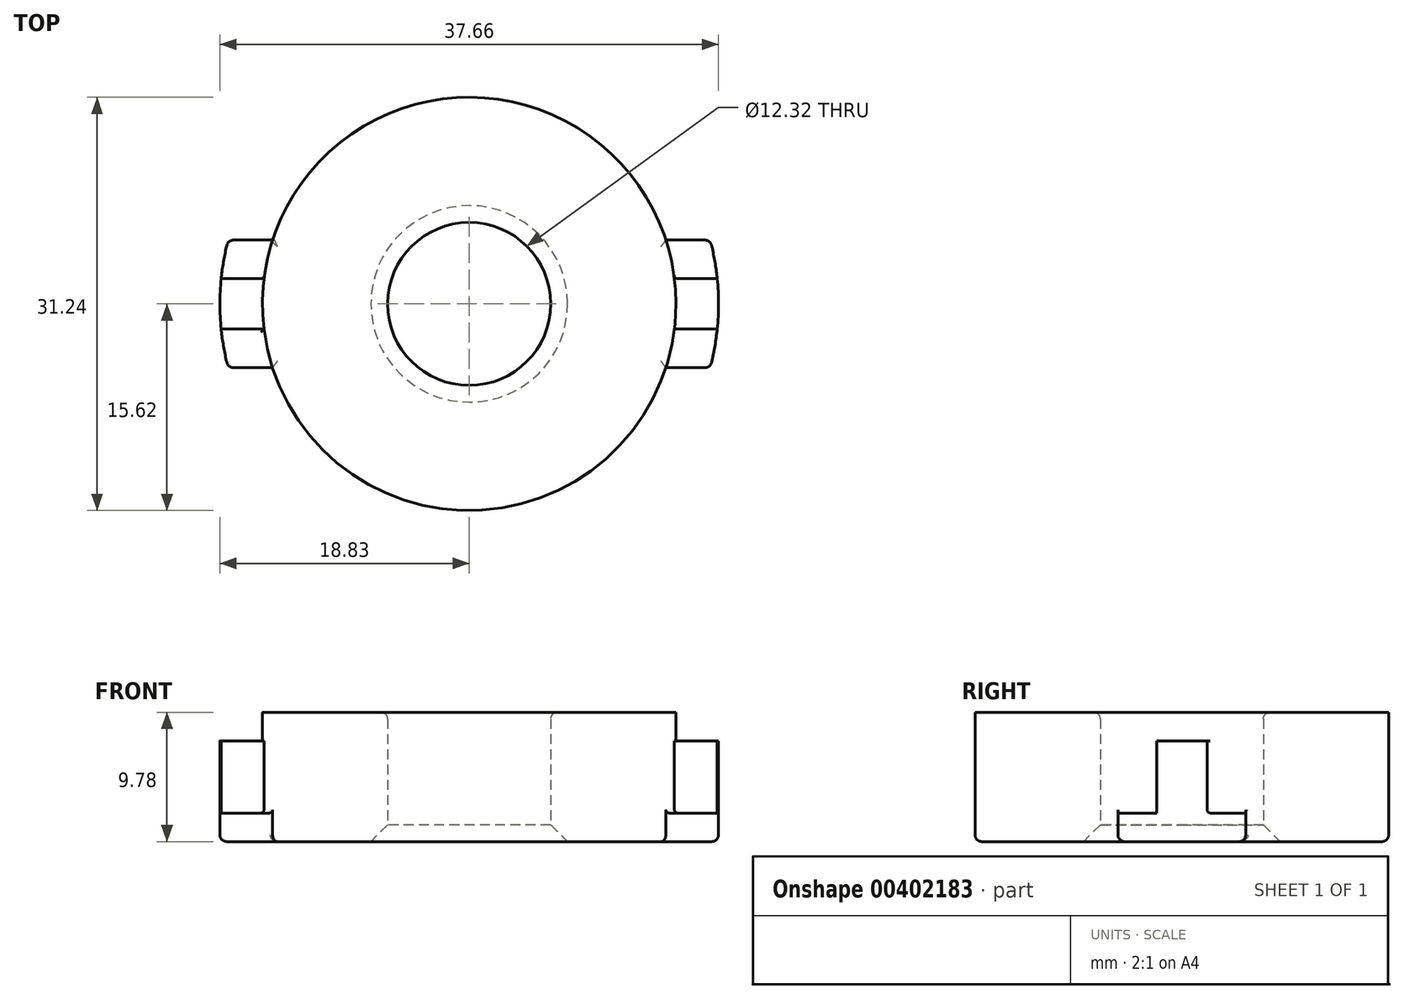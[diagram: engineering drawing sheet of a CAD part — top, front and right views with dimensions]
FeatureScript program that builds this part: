
annotation { "Feature Type Name" : "Feature", "Feature Type Description" : "" }
export const myFeature = defineFeature(function(context is Context, id is Id, definition is map)
    precondition{}
    {
        {
            var Q0;
            Q0=qCreatedBy(makeId("Top.planeOp"),FACE);
            var sketch = newSketch(context, id + "F0", { "sketchPlane" : qUnion([Q0])});
            skArc(sketch, "E0", {"start": v(-14.86, -4.83) * mm, "mid": v(0, -15.62) * mm, "end": v(14.86, -4.83) * mm});
            skCircle(sketch, "E1", {"center": v(0, 0) * mm, "radius": 6.16 * mm});
            skCircle(sketch, "E2", {"center": v(0, 0) * mm, "radius": 18.83 * mm, "construction": true});
            skLineSegment(sketch, "E3", {"start": v(-18.2, 4.83) * mm, "end": v(-14.86, 4.83) * mm});
            skLineSegment(sketch, "E4", {"start": v(-18.2, -4.83) * mm, "end": v(-14.86, -4.83) * mm});
            skArc(sketch, "E5", {"start": v(-18.2, 4.83) * mm, "mid": v(-18.83, 0) * mm, "end": v(-18.2, -4.83) * mm});
            skLineSegment(sketch, "E6.MirrorCS", {"start": v(18.2, 4.83) * mm, "end": v(14.86, 4.83) * mm});
            skLineSegment(sketch, "E7.MirrorCS", {"start": v(18.2, -4.83) * mm, "end": v(14.86, -4.83) * mm});
            skArc(sketch, "E8.MirrorCS", {"start": v(18.2, 4.83) * mm, "mid": v(18.83, 0) * mm, "end": v(18.2, -4.83) * mm});
            skArc(sketch, "E9.trimOffspring", {"start": v(14.86, 4.83) * mm, "mid": v(0, 15.62) * mm, "end": v(-14.86, 4.83) * mm});
            skSolve(sketch);
        }
        {
            var Q0;
            Q0=makeQuery(id+"F0.imprint","IMPRINT",FACE,{"disambiguationData":[TD([[makeQuery(id+"F0.imprint","IMPRINT",EDGE,{"derivedFrom":sQuery(id+"F0.wireOp",EDGE,"E0")}),1.0]])]});
            extrude(context, id + "F1", {"entities" : qUnion([Q0]), "depth" : 9.78 * mm});
        }
        {
            var Q0;
            Q0=makeQuery(id+"F1.opExtrude","CAP_FACE",FACE,{"disambiguationData":[OSD([sQuery(id+"F0.wireOp",EDGE,"E0"),sQuery(id+"F0.wireOp",EDGE,"E1"),sQuery(id+"F0.wireOp",EDGE,"E3"),sQuery(id+"F0.wireOp",EDGE,"E4"),sQuery(id+"F0.wireOp",EDGE,"E5"),sQuery(id+"F0.wireOp",EDGE,"E6.MirrorCS"),sQuery(id+"F0.wireOp",EDGE,"E7.MirrorCS"),sQuery(id+"F0.wireOp",EDGE,"E8.MirrorCS"),sQuery(id+"F0.wireOp",EDGE,"E9.trimOffspring")])],"isStart":false});
            var sketch = newSketch(context, id + "F2", { "sketchPlane" : qUnion([Q0])});
            skCircle(sketch, "E10", {"center": v(0, 0) * mm, "radius": 15.62 * mm});
            skCircle(sketch, "E11", {"center": v(0, 0) * mm, "radius": 21.37 * mm});
            skSolve(sketch);
        }
        {
            var Q0;
            {var subQ2=makeQuery(id+"F1.opExtrude","CAP_EDGE",EDGE,{"disambiguationData":[OSD([sQuery(id+"F0.wireOp",EDGE,"E3")])],"isStart":false});Q0=makeQuery(id+"F2.imprint","IMPRINT",FACE,{"disambiguationData":[TD([[makeQuery(id+"F2.imprint","IMPRINT",EDGE,{"derivedFrom":subQ2}),-1.0]])]});}
            var Q1;
            {var subQ2=makeQuery(id+"F1.opExtrude","CAP_EDGE",EDGE,{"disambiguationData":[OSD([sQuery(id+"F0.wireOp",EDGE,"E6.MirrorCS")])],"isStart":false});Q1=makeQuery(id+"F2.imprint","IMPRINT",FACE,{"disambiguationData":[TD([[makeQuery(id+"F2.imprint","IMPRINT",EDGE,{"derivedFrom":subQ2}),1.0]])]});}
            extrude(context, id + "F3", {"entities" : qUnion([Q0, Q1]), "operationType" : NewBodyOperationType.REMOVE, "oppositeDirection" : true, "depth" : 2.16 * mm});
        }
        {
            var Q0;
            Q0=makeQuery(id+"F3.boolean.opBoolean","COPY",FACE,{"derivedFrom":makeQuery(id+"F3.opExtrude","CAP_FACE",FACE,{"disambiguationData":[OSD([sQuery(id+"F0.wireOp",EDGE,"E3"),sQuery(id+"F0.wireOp",EDGE,"E4"),sQuery(id+"F0.wireOp",EDGE,"E5"),sQuery(id+"F2.wireOp",EDGE,"E10")])],"isStart":false})});
            var sketch = newSketch(context, id + "F4", { "sketchPlane" : qUnion([Q0])});
            skLineSegment(sketch, "E12", {"start": v(-15.5, 1.9) * mm, "end": v(-18.74, 1.9) * mm});
            skLineSegment(sketch, "E13", {"start": v(-15.5, -1.9) * mm, "end": v(-18.74, -1.9) * mm});
            skLineSegment(sketch, "E14.MirrorCS", {"start": v(15.5, 1.9) * mm, "end": v(18.74, 1.9) * mm});
            skLineSegment(sketch, "E15.MirrorCS", {"start": v(15.5, -1.9) * mm, "end": v(18.74, -1.9) * mm});
            skArc(sketch, "E16.0", {"start": v(18.2, 4.83) * mm, "mid": v(18.83, 0) * mm, "end": v(18.2, -4.83) * mm});
            skArc(sketch, "E16.1", {"start": v(14.86, -4.83) * mm, "mid": v(15.62, 0) * mm, "end": v(14.86, 4.83) * mm});
            skLineSegment(sketch, "E17.2", {"start": v(18.2, -4.83) * mm, "end": v(14.86, -4.83) * mm});
            skLineSegment(sketch, "E18.0", {"start": v(18.2, 4.83) * mm, "end": v(14.86, 4.83) * mm});
            skSolve(sketch);
        }
        {
            var Q0;
            {var subQ0=sQuery(id+"F4.wireOp",EDGE,"E14.MirrorCS");Q0=makeQuery(id+"F4.imprint","IMPRINT",FACE,{"disambiguationData":[TD([[makeQuery(id+"F4.imprint","IMPRINT",EDGE,{"derivedFrom":subQ0}),1.0]])]});}
            var Q1;
            {var subQ0=sQuery(id+"F4.wireOp",EDGE,"E15.MirrorCS");Q1=makeQuery(id+"F4.imprint","IMPRINT",FACE,{"disambiguationData":[TD([[makeQuery(id+"F4.imprint","IMPRINT",EDGE,{"derivedFrom":subQ0}),-1.0]])]});}
            var Q2;
            {var subQ0=sQuery(id+"F4.wireOp",EDGE,"E13");Q2=makeQuery(id+"F4.imprint","IMPRINT",FACE,{"disambiguationData":[TD([[makeQuery(id+"F4.imprint","IMPRINT",EDGE,{"derivedFrom":subQ0}),1.0]])]});}
            var Q3;
            {var subQ0=sQuery(id+"F4.wireOp",EDGE,"E12");Q3=makeQuery(id+"F4.imprint","IMPRINT",FACE,{"disambiguationData":[TD([[makeQuery(id+"F4.imprint","IMPRINT",EDGE,{"derivedFrom":subQ0}),-1.0]])]});}
            extrude(context, id + "F5", {"entities" : qUnion([Q0, Q1, Q2, Q3]), "operationType" : NewBodyOperationType.REMOVE, "oppositeDirection" : true, "depth" : 5.46 * mm});
        }
        {
            var Q0;
            Q0=makeQuery(id+"F3.boolean.opBoolean","COPY",EDGE,{"derivedFrom":makeQuery(id+"F3.opExtrude","CAP_EDGE",EDGE,{"disambiguationData":[OSD([sQuery(id+"F0.wireOp",EDGE,"E5")])],"isStart":false})});
            var Q1;
            Q1=makeQuery(id+"F5.boolean.opBoolean","COPY",EDGE,{"derivedFrom":makeQuery(id+"F5.opExtrude","CAP_EDGE",EDGE,{"disambiguationData":[OSD([sQuery(id+"F4.wireOp",EDGE,"E13")])],"isStart":true})});
            var Q2;
            Q2=makeQuery(id+"F5.boolean.opBoolean","COPY",EDGE,{"derivedFrom":makeQuery(id+"F5.opExtrude","CAP_EDGE",EDGE,{"disambiguationData":[OSD([sQuery(id+"F4.wireOp",EDGE,"E12")])],"isStart":true})});
            var Q3;
            Q3=makeQuery(id+"F5.boolean.opBoolean","COPY",EDGE,{"derivedFrom":makeQuery(id+"F5.opExtrude","SWEPT_EDGE",EDGE,{"disambiguationData":[OSD([sQuery(id+"F0.wireOp",EDGE,"E5"),sQuery(id+"F4.wireOp",EDGE,"E13")])]})});
            var Q4;
            {var subQ0=sQuery(id+"F0.wireOp",EDGE,"E5");var subQ1=makeQuery(id+"F3.boolean.opBoolean","COPY",EDGE,{"derivedFrom":makeQuery(id+"F3.opExtrude","CAP_EDGE",EDGE,{"disambiguationData":[OSD([subQ0])],"isStart":false})});Q4=makeQuery(id+"F5.boolean.opBoolean","COPY",EDGE,{"derivedFrom":makeQuery(id+"F5.opExtrude","CAP_EDGE",EDGE,{"disambiguationData":[OSD([subQ0]),TDD([makeQuery(id+"F4.imprint","IMPRINT",EDGE,{"disambiguationData":[TD([[makeQuery(id+"F4.imprint","INTERSECT",VERTEX,{"derivedFrom":[makeQuery(id+"F3.boolean.opBoolean","COPY",EDGE,{"derivedFrom":makeQuery(id+"F3.opExtrude","CAP_EDGE",EDGE,{"disambiguationData":[OSD([sQuery(id+"F0.wireOp",EDGE,"E4")])],"isStart":false})}),subQ1]}),1.0]])],"derivedFrom":subQ1})])],"isStart":false})});}
            var Q5;
            Q5=makeQuery(id+"F1.opExtrude","SWEPT_EDGE",EDGE,{"disambiguationData":[OSD([sQuery(id+"F0.wireOp",EDGE,"E4"),sQuery(id+"F0.wireOp",EDGE,"E5")])]});
            var Q6;
            Q6=makeQuery(id+"F5.boolean.opBoolean","COPY",EDGE,{"derivedFrom":makeQuery(id+"F5.opExtrude","CAP_EDGE",EDGE,{"disambiguationData":[OSD([sQuery(id+"F0.wireOp",EDGE,"E4")])],"isStart":false})});
            var Q7;
            Q7=makeQuery(id+"F1.opExtrude","CAP_EDGE",EDGE,{"disambiguationData":[OSD([sQuery(id+"F0.wireOp",EDGE,"E4")])],"isStart":true});
            var Q8;
            Q8=makeQuery(id+"F1.opExtrude","CAP_EDGE",EDGE,{"disambiguationData":[OSD([sQuery(id+"F0.wireOp",EDGE,"E5")])],"isStart":true});
            var Q9;
            Q9=makeQuery(id+"F1.opExtrude","CAP_EDGE",EDGE,{"disambiguationData":[OSD([sQuery(id+"F0.wireOp",EDGE,"E3")])],"isStart":true});
            var Q10;
            Q10=makeQuery(id+"F1.opExtrude","CAP_EDGE",EDGE,{"disambiguationData":[OSD([sQuery(id+"F0.wireOp",EDGE,"E9.trimOffspring")])],"isStart":true});
            var Q11;
            Q11=makeQuery(id+"F1.opExtrude","SWEPT_EDGE",EDGE,{"disambiguationData":[OSD([sQuery(id+"F0.wireOp",EDGE,"E3"),sQuery(id+"F0.wireOp",EDGE,"E5")])]});
            var Q12;
            Q12=makeQuery(id+"F5.boolean.opBoolean","COPY",EDGE,{"derivedFrom":makeQuery(id+"F5.opExtrude","SWEPT_EDGE",EDGE,{"disambiguationData":[OSD([sQuery(id+"F0.wireOp",EDGE,"E5"),sQuery(id+"F4.wireOp",EDGE,"E12")])]})});
            var Q13;
            Q13=makeQuery(id+"F1.opExtrude","CAP_EDGE",EDGE,{"disambiguationData":[OSD([sQuery(id+"F0.wireOp",EDGE,"E0")])],"isStart":true});
            var Q14;
            {var subQ0=sQuery(id+"F2.wireOp",EDGE,"E10");Q14=makeQuery(id+"F3.boolean.opBoolean","MERGE",EDGE,{"derivedFrom":[makeQuery(id+"F1.opExtrude","CAP_EDGE",EDGE,{"disambiguationData":[OSD([sQuery(id+"F0.wireOp",EDGE,"E0")])],"isStart":false}),makeQuery(id+"F1.opExtrude","CAP_EDGE",EDGE,{"disambiguationData":[OSD([sQuery(id+"F0.wireOp",EDGE,"E9.trimOffspring")])],"isStart":false}),makeQuery(id+"F3.opExtrude","CAP_EDGE",EDGE,{"disambiguationData":[OSD([subQ0]),TDD([makeQuery(id+"F2.imprint","IMPRINT",EDGE,{"disambiguationData":[TD([[makeQuery(id+"F2.imprint","INTERSECT",VERTEX,{"derivedFrom":[makeQuery(id+"F1.opExtrude","CAP_EDGE",EDGE,{"disambiguationData":[OSD([sQuery(id+"F0.wireOp",EDGE,"E4")])],"isStart":false}),subQ0]}),1.0]])],"derivedFrom":subQ0})])],"isStart":true}),makeQuery(id+"F3.opExtrude","CAP_EDGE",EDGE,{"disambiguationData":[OSD([subQ0]),TDD([makeQuery(id+"F2.imprint","IMPRINT",EDGE,{"disambiguationData":[TD([[makeQuery(id+"F2.imprint","INTERSECT",VERTEX,{"derivedFrom":[makeQuery(id+"F1.opExtrude","CAP_EDGE",EDGE,{"disambiguationData":[OSD([sQuery(id+"F0.wireOp",EDGE,"E7.MirrorCS")])],"isStart":false}),subQ0]}),-1.0]])],"derivedFrom":subQ0})])],"isStart":true})]});}
            var Q15;
            Q15=makeQuery(id+"F1.opExtrude","CAP_EDGE",EDGE,{"disambiguationData":[OSD([sQuery(id+"F0.wireOp",EDGE,"E7.MirrorCS")])],"isStart":true});
            var Q16;
            Q16=makeQuery(id+"F1.opExtrude","SWEPT_EDGE",EDGE,{"disambiguationData":[OSD([sQuery(id+"F0.wireOp",EDGE,"E7.MirrorCS"),sQuery(id+"F0.wireOp",EDGE,"E8.MirrorCS")])]});
            var Q17;
            {var subQ0=sQuery(id+"F4.wireOp",EDGE,"E16.0");Q17=makeQuery(id+"F5.boolean.opBoolean","COPY",EDGE,{"derivedFrom":makeQuery(id+"F5.opExtrude","CAP_EDGE",EDGE,{"disambiguationData":[OSD([subQ0]),TDD([makeQuery(id+"F4.imprint","IMPRINT",EDGE,{"disambiguationData":[TD([[makeQuery(id+"F4.imprint","INTERSECT",VERTEX,{"derivedFrom":[sQuery(id+"F4.wireOp",EDGE,"E15.MirrorCS"),subQ0]}),-1.0]])],"derivedFrom":subQ0})])],"isStart":false})});}
            var Q18;
            Q18=makeQuery(id+"F5.boolean.opBoolean","COPY",EDGE,{"derivedFrom":makeQuery(id+"F5.opExtrude","SWEPT_EDGE",EDGE,{"disambiguationData":[OSD([sQuery(id+"F4.wireOp",EDGE,"E15.MirrorCS"),sQuery(id+"F4.wireOp",EDGE,"E16.0")])]})});
            var Q19;
            Q19=makeQuery(id+"F3.boolean.opBoolean","COPY",EDGE,{"derivedFrom":makeQuery(id+"F3.opExtrude","CAP_EDGE",EDGE,{"disambiguationData":[OSD([sQuery(id+"F0.wireOp",EDGE,"E8.MirrorCS")])],"isStart":false})});
            var Q20;
            Q20=makeQuery(id+"F5.boolean.opBoolean","COPY",EDGE,{"derivedFrom":makeQuery(id+"F5.opExtrude","SWEPT_EDGE",EDGE,{"disambiguationData":[OSD([sQuery(id+"F4.wireOp",EDGE,"E14.MirrorCS"),sQuery(id+"F4.wireOp",EDGE,"E16.0")])]})});
            var Q21;
            {var subQ0=sQuery(id+"F4.wireOp",EDGE,"E16.0");Q21=makeQuery(id+"F5.boolean.opBoolean","COPY",EDGE,{"derivedFrom":makeQuery(id+"F5.opExtrude","CAP_EDGE",EDGE,{"disambiguationData":[OSD([subQ0]),TDD([makeQuery(id+"F4.imprint","IMPRINT",EDGE,{"disambiguationData":[TD([[makeQuery(id+"F4.imprint","INTERSECT",VERTEX,{"derivedFrom":[sQuery(id+"F4.wireOp",EDGE,"E14.MirrorCS"),subQ0]}),1.0]])],"derivedFrom":subQ0})])],"isStart":false})});}
            var Q22;
            Q22=makeQuery(id+"F1.opExtrude","SWEPT_EDGE",EDGE,{"disambiguationData":[OSD([sQuery(id+"F0.wireOp",EDGE,"E6.MirrorCS"),sQuery(id+"F0.wireOp",EDGE,"E8.MirrorCS")])]});
            var Q23;
            Q23=makeQuery(id+"F1.opExtrude","CAP_EDGE",EDGE,{"disambiguationData":[OSD([sQuery(id+"F0.wireOp",EDGE,"E8.MirrorCS")])],"isStart":true});
            var Q24;
            Q24=makeQuery(id+"F5.boolean.opBoolean","COPY",EDGE,{"derivedFrom":makeQuery(id+"F5.opExtrude","CAP_EDGE",EDGE,{"disambiguationData":[OSD([sQuery(id+"F4.wireOp",EDGE,"E15.MirrorCS")])],"isStart":true})});
            var Q25;
            Q25=makeQuery(id+"F5.boolean.opBoolean","COPY",EDGE,{"derivedFrom":makeQuery(id+"F5.opExtrude","CAP_EDGE",EDGE,{"disambiguationData":[OSD([sQuery(id+"F4.wireOp",EDGE,"E14.MirrorCS")])],"isStart":true})});
            var Q26;
            Q26=makeQuery(id+"F5.boolean.opBoolean","COPY",EDGE,{"derivedFrom":makeQuery(id+"F5.opExtrude","CAP_EDGE",EDGE,{"disambiguationData":[OSD([sQuery(id+"F4.wireOp",EDGE,"E18.0")])],"isStart":false})});
            var Q27;
            Q27=makeQuery(id+"F1.opExtrude","CAP_EDGE",EDGE,{"disambiguationData":[OSD([sQuery(id+"F0.wireOp",EDGE,"E6.MirrorCS")])],"isStart":true});
            var Q28;
            Q28=makeQuery(id+"F5.boolean.opBoolean","COPY",EDGE,{"derivedFrom":makeQuery(id+"F5.opExtrude","CAP_EDGE",EDGE,{"disambiguationData":[OSD([sQuery(id+"F0.wireOp",EDGE,"E3")])],"isStart":false})});
            var Q29;
            {var subQ0=sQuery(id+"F0.wireOp",EDGE,"E5");var subQ1=makeQuery(id+"F3.boolean.opBoolean","COPY",EDGE,{"derivedFrom":makeQuery(id+"F3.opExtrude","CAP_EDGE",EDGE,{"disambiguationData":[OSD([subQ0])],"isStart":false})});Q29=makeQuery(id+"F5.boolean.opBoolean","COPY",EDGE,{"derivedFrom":makeQuery(id+"F5.opExtrude","CAP_EDGE",EDGE,{"disambiguationData":[OSD([subQ0]),TDD([makeQuery(id+"F4.imprint","IMPRINT",EDGE,{"disambiguationData":[TD([[makeQuery(id+"F4.imprint","INTERSECT",VERTEX,{"derivedFrom":[makeQuery(id+"F3.boolean.opBoolean","COPY",EDGE,{"derivedFrom":makeQuery(id+"F3.opExtrude","CAP_EDGE",EDGE,{"disambiguationData":[OSD([sQuery(id+"F0.wireOp",EDGE,"E3")])],"isStart":false})}),subQ1]}),-1.0]])],"derivedFrom":subQ1})])],"isStart":false})});}
            var Q30;
            Q30=makeQuery(id+"F1.opExtrude","CAP_EDGE",EDGE,{"disambiguationData":[OSD([sQuery(id+"F0.wireOp",EDGE,"E1")])],"isStart":false});
            var Q31;
            Q31=makeQuery(id+"F5.boolean.opBoolean","COPY",EDGE,{"derivedFrom":makeQuery(id+"F5.opExtrude","CAP_EDGE",EDGE,{"disambiguationData":[OSD([sQuery(id+"F4.wireOp",EDGE,"E17.2")])],"isStart":false})});
            fillet(context, id + "F6", {"entities" : qUnion([Q0, Q1, Q2, Q3, Q4, Q5, Q6, Q7, Q8, Q9, Q10, Q11, Q12, Q13, Q14, Q15, Q16, Q17, Q18, Q19, Q20, Q21, Q22, Q23, Q24, Q25, Q26, Q27, Q28, Q29, Q30, Q31]), "radius" : 0.5 * mm, "tangentPropagation" : true, "allowEdgeOverflow" : false});
        }
        {
            var Q0;
            {var subQ0=sQuery(id+"F4.wireOp",EDGE,"E16.1");Q0=makeQuery(id+"F5.boolean.opBoolean","COPY",EDGE,{"derivedFrom":makeQuery(id+"F5.opExtrude","CAP_EDGE",EDGE,{"disambiguationData":[OSD([subQ0]),TDD([makeQuery(id+"F4.imprint","IMPRINT",EDGE,{"disambiguationData":[TD([[makeQuery(id+"F4.imprint","INTERSECT",VERTEX,{"derivedFrom":[sQuery(id+"F4.wireOp",EDGE,"E14.MirrorCS"),subQ0]}),-1.0]])],"derivedFrom":subQ0})])],"isStart":false})});}
            var Q1;
            Q1=makeQuery(id+"F5.boolean.opBoolean","COPY",EDGE,{"derivedFrom":makeQuery(id+"F5.opExtrude","CAP_EDGE",EDGE,{"disambiguationData":[OSD([sQuery(id+"F4.wireOp",EDGE,"E14.MirrorCS")])],"isStart":false})});
            var Q2;
            Q2=makeQuery(id+"F5.boolean.opBoolean","COPY",EDGE,{"derivedFrom":makeQuery(id+"F5.opExtrude","SWEPT_EDGE",EDGE,{"disambiguationData":[OSD([sQuery(id+"F4.wireOp",EDGE,"E14.MirrorCS"),sQuery(id+"F4.wireOp",EDGE,"E16.1")])]})});
            var Q3;
            {var subQ0=sQuery(id+"F4.wireOp",EDGE,"E16.1");Q3=makeQuery(id+"F5.boolean.opBoolean","COPY",EDGE,{"derivedFrom":makeQuery(id+"F5.opExtrude","CAP_EDGE",EDGE,{"disambiguationData":[OSD([subQ0]),TDD([makeQuery(id+"F4.imprint","IMPRINT",EDGE,{"disambiguationData":[TD([[makeQuery(id+"F4.imprint","INTERSECT",VERTEX,{"derivedFrom":[sQuery(id+"F4.wireOp",EDGE,"E15.MirrorCS"),subQ0]}),1.0]])],"derivedFrom":subQ0})])],"isStart":false})});}
            var Q4;
            Q4=makeQuery(id+"F1.opExtrude","SWEPT_EDGE",EDGE,{"disambiguationData":[OSD([sQuery(id+"F0.wireOp",EDGE,"E3"),sQuery(id+"F0.wireOp",EDGE,"E9.trimOffspring")])]});
            var Q5;
            Q5=makeQuery(id+"F5.boolean.opBoolean","COPY",EDGE,{"derivedFrom":makeQuery(id+"F5.opExtrude","CAP_EDGE",EDGE,{"disambiguationData":[OSD([sQuery(id+"F4.wireOp",EDGE,"E12")])],"isStart":false})});
            var Q6;
            Q6=makeQuery(id+"F5.boolean.opBoolean","COPY",EDGE,{"derivedFrom":makeQuery(id+"F5.opExtrude","SWEPT_EDGE",EDGE,{"disambiguationData":[OSD([sQuery(id+"F2.wireOp",EDGE,"E10"),sQuery(id+"F4.wireOp",EDGE,"E12")])]})});
            var Q7;
            Q7=makeQuery(id+"F5.boolean.opBoolean","COPY",EDGE,{"derivedFrom":makeQuery(id+"F5.opExtrude","CAP_EDGE",EDGE,{"disambiguationData":[OSD([sQuery(id+"F4.wireOp",EDGE,"E13")])],"isStart":false})});
            var Q8;
            {var subQ0=sQuery(id+"F0.wireOp",EDGE,"E4");var subQ1=sQuery(id+"F2.wireOp",EDGE,"E10");var subQ2=makeQuery(id+"F3.boolean.opBoolean","COPY",EDGE,{"derivedFrom":makeQuery(id+"F3.opExtrude","CAP_EDGE",EDGE,{"disambiguationData":[OSD([subQ1]),TDD([makeQuery(id+"F2.imprint","IMPRINT",EDGE,{"disambiguationData":[TD([[makeQuery(id+"F2.imprint","INTERSECT",VERTEX,{"derivedFrom":[makeQuery(id+"F1.opExtrude","CAP_EDGE",EDGE,{"disambiguationData":[OSD([subQ0])],"isStart":false}),subQ1]}),1.0]])],"derivedFrom":subQ1})])],"isStart":false})});Q8=makeQuery(id+"F5.boolean.opBoolean","COPY",EDGE,{"derivedFrom":makeQuery(id+"F5.opExtrude","CAP_EDGE",EDGE,{"disambiguationData":[OSD([subQ1]),TDD([makeQuery(id+"F4.imprint","IMPRINT",EDGE,{"disambiguationData":[TD([[makeQuery(id+"F4.imprint","INTERSECT",VERTEX,{"derivedFrom":[subQ2,makeQuery(id+"F3.boolean.opBoolean","COPY",EDGE,{"derivedFrom":makeQuery(id+"F3.opExtrude","CAP_EDGE",EDGE,{"disambiguationData":[OSD([subQ0])],"isStart":false})})]}),1.0]])],"derivedFrom":subQ2})])],"isStart":false})});}
            fillet(context, id + "F7", {"entities" : qUnion([Q0, Q1, Q2, Q3, Q4, Q5, Q6, Q7, Q8]), "radius" : 0.25 * mm, "tangentPropagation" : true, "allowEdgeOverflow" : false});
        }
        {
            var Q0;
            Q0=makeQuery(id+"F1.opExtrude","CAP_EDGE",EDGE,{"disambiguationData":[OSD([sQuery(id+"F0.wireOp",EDGE,"E1")])],"isStart":true});
            chamfer(context, id + "F8", {"entities" : qUnion([Q0]), "width" : 1.27 * mm, "tangentPropagation" : true});
        }
    });
